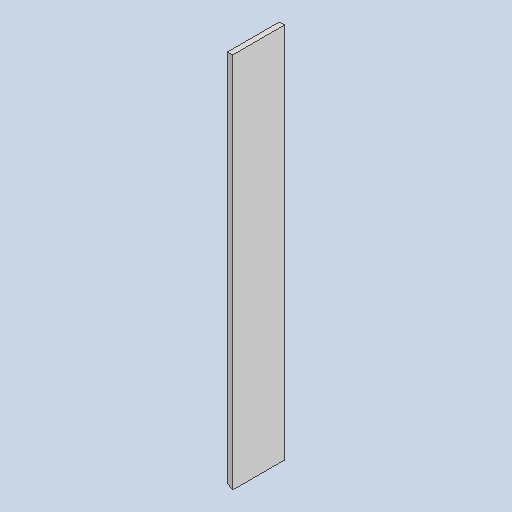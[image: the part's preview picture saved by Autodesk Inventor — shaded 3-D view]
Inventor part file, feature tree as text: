
AUTODESK INVENTOR PART (.ipt)
format: ipt  version: 2025 (Build 290162010, 162A)  size: 91,648 bytes
history: native  units: mm
features: extrude x1, sketch x1
ambient origin geometry x8: Origin, YZ Plane, XZ Plane, XY Plane, X Axis, Y Axis, Z Axis, Center Point
bodies: Solid1 (feature_tree)
feature tree (2):
  extrude  "Extrusion1"  Depth=80.0mm
  sketch  "Sketch1"  dims[d0=513.0mm d1=260.0mm d2=635.0mm d10=5.0mm d11=8.0mm d12=80.0mm d13=0.0mm]
